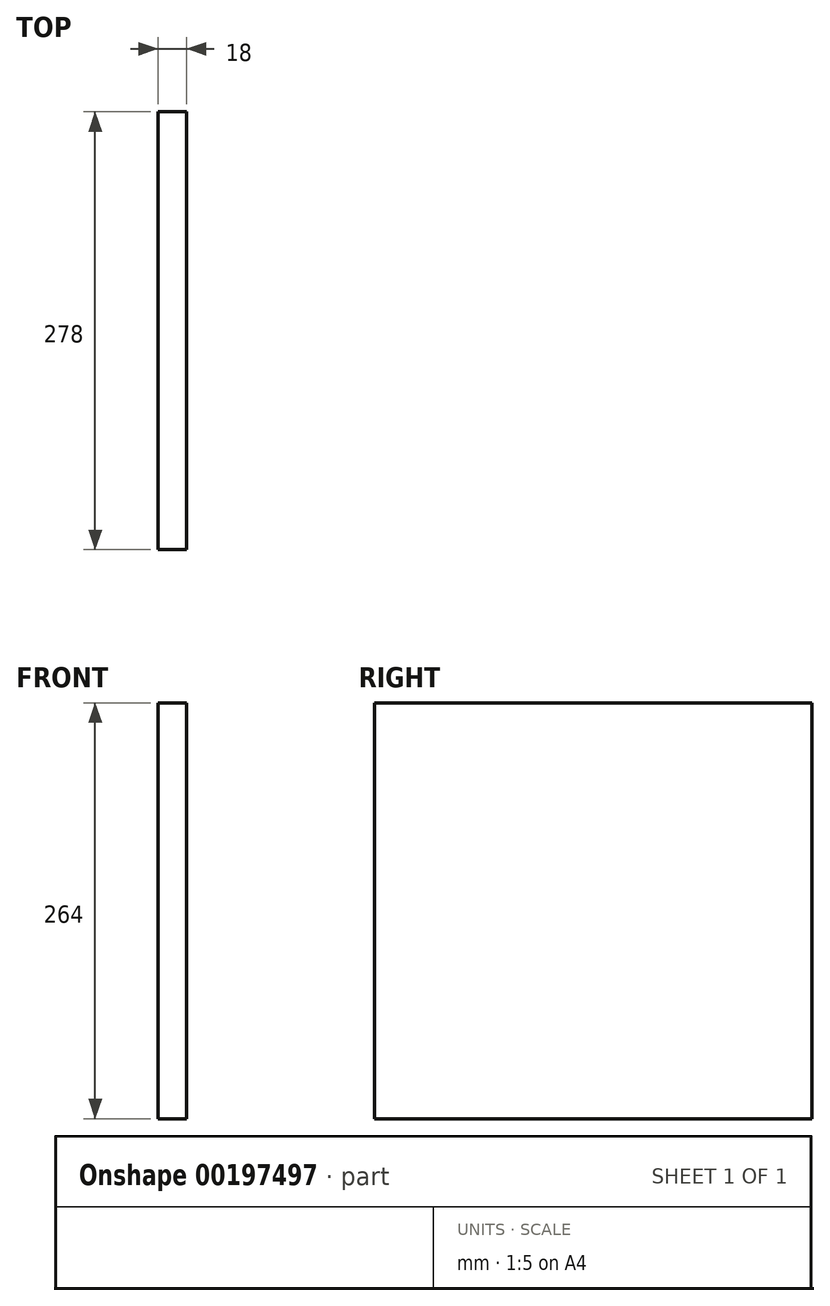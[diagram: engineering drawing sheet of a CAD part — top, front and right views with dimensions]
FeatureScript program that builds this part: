
annotation { "Feature Type Name" : "Feature", "Feature Type Description" : "" }
export const myFeature = defineFeature(function(context is Context, id is Id, definition is map)
    precondition{}
    {
        {
            var Q0;
            Q0=qCreatedBy(makeId("Right.planeOp"),FACE);
            var sketch = newSketch(context, id + "F0", { "sketchPlane" : qUnion([Q0])});
            skLineSegment(sketch, "E0.bottom", {"start": v(139, 132) * mm, "end": v(-139, 132) * mm});
            skLineSegment(sketch, "E0.top", {"start": v(139, -132) * mm, "end": v(-139, -132) * mm});
            skLineSegment(sketch, "E0.left", {"start": v(139, 132) * mm, "end": v(139, -132) * mm});
            skLineSegment(sketch, "E0.right", {"start": v(-139, 132) * mm, "end": v(-139, -132) * mm});
            skPoint(sketch, "E0.middle", {"position": v(0, 0) * mm});
            skSolve(sketch);
        }
        {
            var Q0;
            Q0 = qSketchRegion(id + "F0", true);
            extrude(context, id + "F1", {"entities" : qUnion([Q0]), "depth" : 18 * mm});
        }
    });
